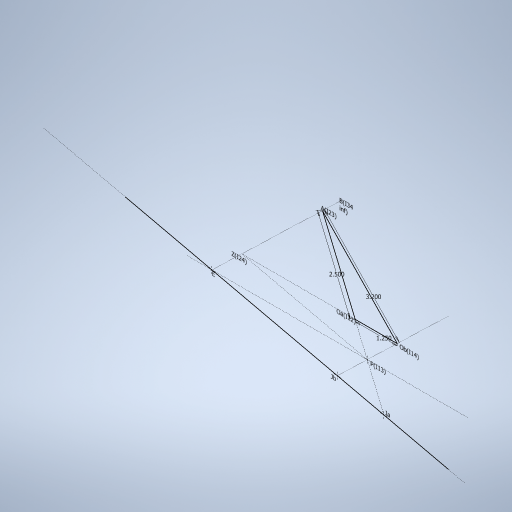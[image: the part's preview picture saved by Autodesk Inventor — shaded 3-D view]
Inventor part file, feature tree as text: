
AUTODESK INVENTOR PART (.ipt)
format: ipt  version: 2024 (Build 280153000, 153)  size: 249,856 bytes
history: native  units: in
note: dims shown in document units (in); Inventor stores cm internally (conversion verified against a paired STEP export)
features: sketch x1
ambient origin geometry x8: Origin, YZ Plane, XZ Plane, XY Plane, X Axis, Y Axis, Z Axis, Center Point
feature tree (1):
  sketch  "Sketch1"  dims[d0=1.25in d1=2.5in d2=3.2in]
